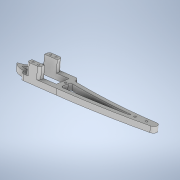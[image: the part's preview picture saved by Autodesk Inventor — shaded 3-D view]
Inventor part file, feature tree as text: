
AUTODESK INVENTOR PART (.ipt)
format: ipt  version: 2020.3 (Build 243373000, 373)  size: 239,616 bytes
history: native  units: mm
features: fillet x5, hole x3, sketch x2, extrude x2, chamfer x1
ambient origin geometry x8: Origin, YZ Plane, XZ Plane, XY Plane, X Axis, Y Axis, Z Axis, Center Point
bodies: Solid1 (feature_tree)
feature tree (13):
  sketch  "Sketch1"  dims[d4=5.0mm d5=23.0mm]
  extrude  "Extrusion1"  Depth=23.0mm
  chamfer  "Chamfer1"  Distance=5.0mm
  fillet  "Fillet1"  Radius=7.0mm
  fillet  "Fillet2"  Radius=5.0mm
  fillet  "Fillet3"  Radius=4.0mm
  fillet  "Fillet4"  Radius=20.0mm
  hole  "Hole3"  [1 undecoded]
  hole  "Hole4"  [1 undecoded]
  extrude  "Extrusion3"  Depth=5.0mm
  fillet  "Fillet6"  Radius=6.0mm
  hole  "Hole5"  [1 undecoded]
  sketch  "Sketch2"  dims[d6=13.0mm d7=5.0mm d15=7.0mm d17=5.0mm d18=4.0mm d21=20.0mm d23=80.0mm d24=15.0mm d29=29.670597mm d30=6.0mm d31=10.0mm d33=5.0mm d34=0.0mm d37=2.5mm d38=2.0mm d39=45.0deg d40=3.0mm d41=3.0mm d42=2.0mm d43=4.0mm d44=3.0mm d45=4.0mm d50=13.0mm d51=12.0mm d52=22.68928mm d53=16.057029mm d61=0.5mm d69=2.0mm d70=6.0mm d71=4.0mm d72=2.0mm d73=90.0deg d74=5.0mm d75=20.594885mm d76=2.0mm d77=6.0mm d78=4.0mm d79=2.0mm d80=90.0deg d81=5.0mm d82=20.594885mm d83=15.0mm d84=0.0mm d86=2.0mm d87=5.0mm d88=1.8mm d89=6.0mm d90=4.0mm d91=2.0mm d92=90.0deg d93=5.0mm d94=20.594885mm]
note: 3 required parameter values undecoded (feature->parameter linkage not recoverable at this tier; creation-order binding heuristic only, values carry confidence <= 0.55)
